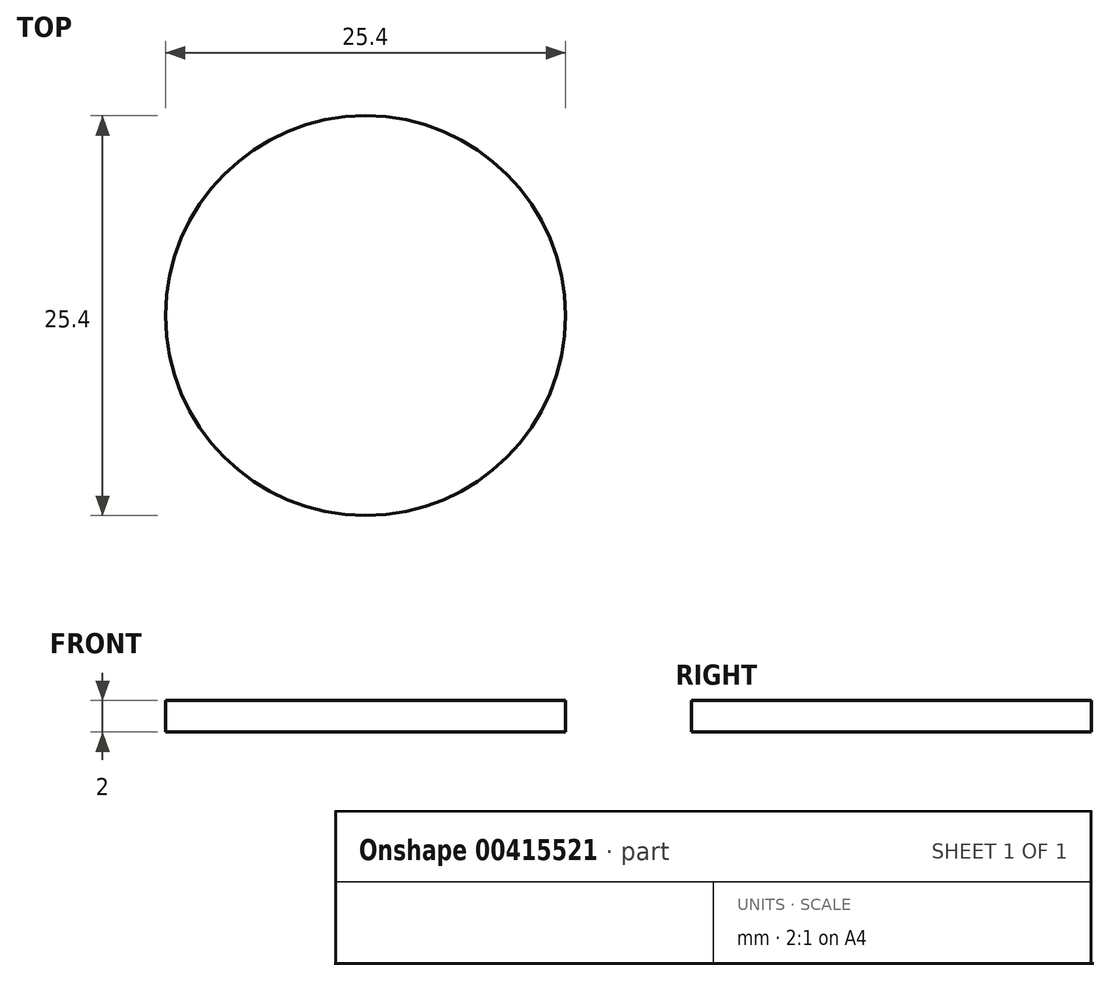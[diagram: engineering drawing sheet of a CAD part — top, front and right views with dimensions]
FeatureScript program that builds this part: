
annotation { "Feature Type Name" : "Feature", "Feature Type Description" : "" }
export const myFeature = defineFeature(function(context is Context, id is Id, definition is map)
    precondition{}
    {
        {
            var Q0;
            Q0=qCreatedBy(makeId("Top.planeOp"),FACE);
            var sketch = newSketch(context, id + "F0", { "sketchPlane" : qUnion([Q0])});
            skCircle(sketch, "E0", {"center": v(0, 0) * mm, "radius": 12.7 * mm});
            skSolve(sketch);
        }
        {
            var Q0;
            Q0 = qSketchRegion(id + "F0", true);
            extrude(context, id + "F1", {"entities" : qUnion([Q0]), "depth" : 2 * mm});
        }
    });
